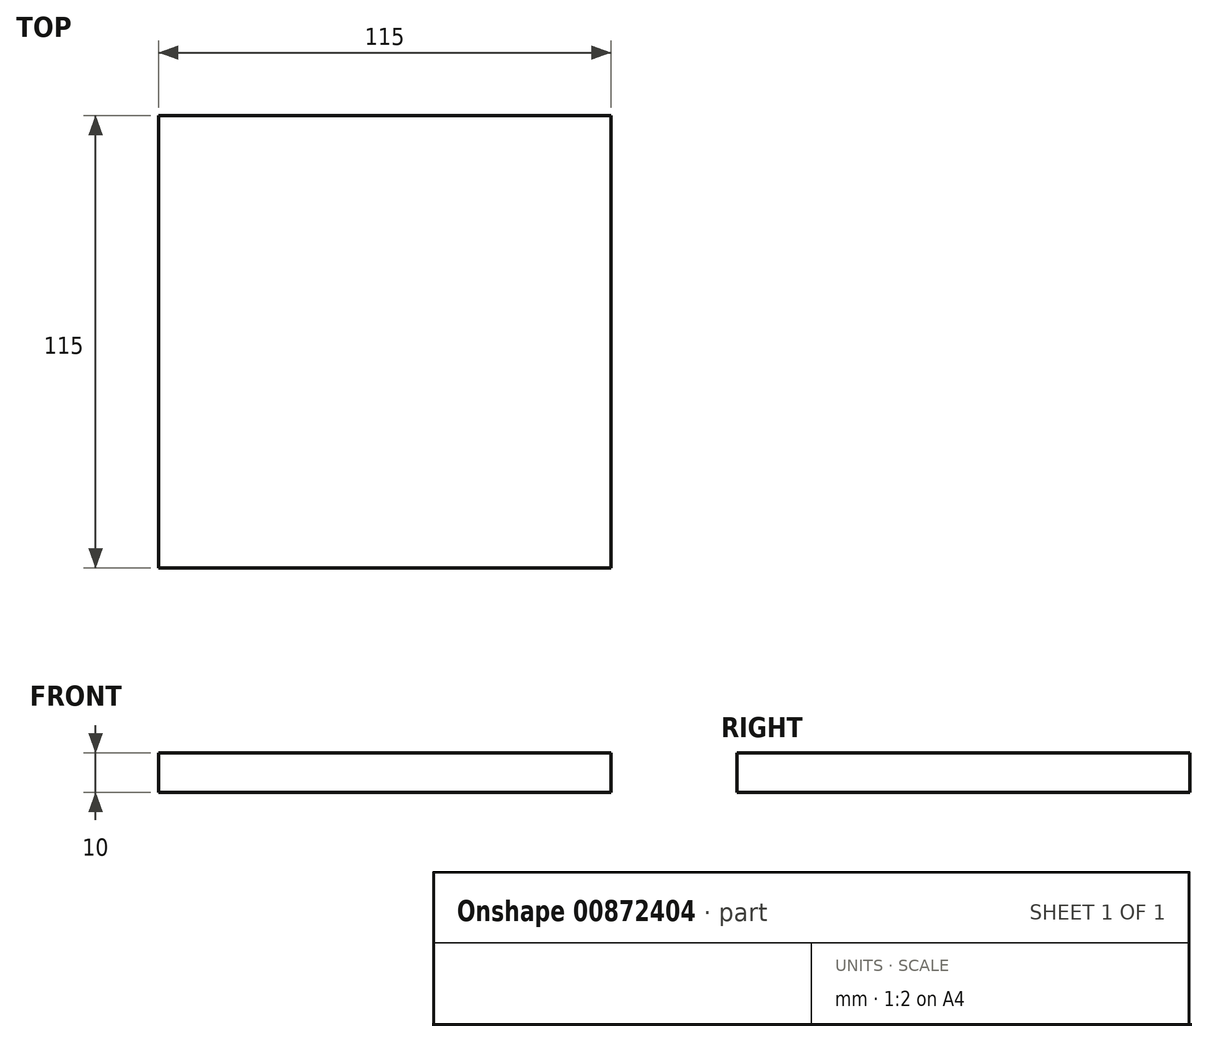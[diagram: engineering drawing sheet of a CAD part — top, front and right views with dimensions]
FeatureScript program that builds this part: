
annotation { "Feature Type Name" : "Feature", "Feature Type Description" : "" }
export const myFeature = defineFeature(function(context is Context, id is Id, definition is map)
    precondition{}
    {
        {
            var Q0;
            Q0=qCreatedBy(makeId("Top.planeOp"),FACE);
            var sketch = newSketch(context, id + "F0", { "sketchPlane" : qUnion([Q0])});
            skLineSegment(sketch, "E0.bottom", {"start": v(-57.5, 57.5) * mm, "end": v(57.5, 57.5) * mm});
            skLineSegment(sketch, "E0.top", {"start": v(-57.5, -57.5) * mm, "end": v(57.5, -57.5) * mm});
            skLineSegment(sketch, "E0.left", {"start": v(-57.5, 57.5) * mm, "end": v(-57.5, -57.5) * mm});
            skLineSegment(sketch, "E0.right", {"start": v(57.5, 57.5) * mm, "end": v(57.5, -57.5) * mm});
            skSolve(sketch);
        }
        {
            var Q0;
            Q0 = qSketchRegion(id + "F0", true);
            extrude(context, id + "F1", {"entities" : qUnion([Q0]), "depth" : 10 * mm, "offsetDistance" : 25 * mm});
        }
    });
